# Revit family: BIMLIB_Конвектор_ВстраиваемыйВПолСПринудительнойКонвекцией_ВКВ70_24В_VITRON
name_source: partatom
category: Оборудование
revit_build: Autodesk Revit 2017 (Build: 20170118_1100(x64)
units: mm (PartAtom-declared; Revit-internal decimal feet)

## family parameters
Всегда вертикально = Да
На основе рабочей плоскости = Нет
Общий = Нет
При загрузке вырезать с полостями = Нет
Размер круглого соединителя = Использовать диаметр
Тип детали = Нормальный
Точка расчета площади = Нет

## types (2) — shared parameters
1 = 1
2 = 2
3 = 3
ADSK_URL документации изделия = https://vitron.ru
ADSK_URL страницы изделия = https://vitron.ru
ADSK_Версия Revit = 2017
ADSK_Единица измерения = шт.
ADSK_Завод-изготовитель = Вилма / VITRON
ADSK_Классификация нагрузок = Прочее
ADSK_Количество фаз = 1
ADSK_Коэффициент мощности = 0.98
ADSK_Размер_Высота = 70 мм
ADSK_Размер_Диаметр = 15 мм
BL_BIM library = https://bimlib.pro
URL = https://vitron.ru
VIT_Максимальная рабочая температура теплоносителя = 95 °C
VIT_Рабочее давление теплоносителя = 1600000.0 Па
VIT_Степень защиты вентилятора = IP20
VIT_Уровень звукового давления от вентилятора = 19/30 дБ(А)
Высота теплообменника = 50 мм
Изготовитель = Вилма / VITRON
Количество труб теплообменника = 2
Материал_Корпуса = BIMLIB_ОцинкованнаяСталь_VITRON
Материал_Решетка = BIMLIB_Алюминий_VITRON
Описание = Встраиваемый в пол конвектор с принудительной конвекцией VITRON - отопительный прибор, в котором установлен медно-алюминиевый теплообменник и тангенциальный вентилятор, тепло от которого передаётся в отапливаемое помещение путём естественной (при выключенном вентиляторе), и принудительной (при включённом вентиляторе) конвекции. Позволяет преградить поток холодного воздуха от застекленных фасадов или окон. Данный тип конвектора служит для отопления только сухих помещений. Применяется в качестве основного отопительного прибора в помещениях с любыми потребностями в интенсивности отопления. Возможно комбинированное использование с системами тёплого пола, вентиляции, радиаторного водяного отопления.
Подключение с торца = Подключение с торца
Подключение сверху = Подключение сверху
Подключение снизу = Подключение снизу
Расстояние между патрубками = 50 мм
Ширина теплообменника = 100 мм

## per-type parameters (varying)
| type | ADSK_Обозначение | ADSK_Размер_Ширина | VIT_Тепловая мощность на 1 м | Коэффициент n |
| Конвектор_Шириной 260мм | ВКВ.70.260 | 260 мм | 292.176 Вт | 1.65 |
| Конвектор_Шириной 300мм | ВКВ.70.300 | 300 мм | 323.027 Вт | 1.6 |
